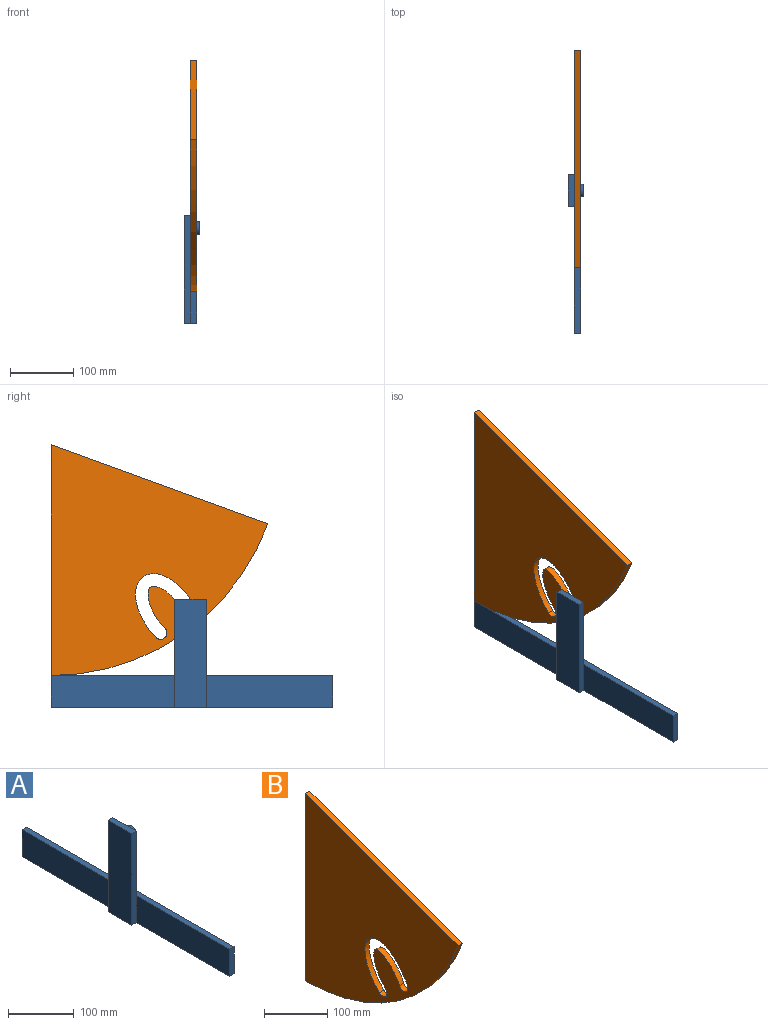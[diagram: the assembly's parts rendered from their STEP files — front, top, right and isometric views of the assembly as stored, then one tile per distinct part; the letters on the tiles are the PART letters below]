
ASSEMBLY  parts=2 mates=1
PART A: 14 faces, bbox 25x444.9x170 mm
  f0: plane 199.88x50mm, normal (-1,0,0), area 9994mm2, adj f2,f3,f4,f8
  f1: plane 50x10mm, normal (0,1,0), area 500mm2, adj f2,f4,f5,f6
  f2: plane 444.88x10mm, normal (0,0,1), area 4448.8mm2, adj f0,f1,f3,f5,f6,f11
  f3: plane 50x10mm, normal (0,-1,0), area 500mm2, adj f0,f2,f4,f6
  f4: plane 444.88x20mm, normal (0,0,-1), area 4948.8mm2, adj f0,f1,f3,f5,f6,f7,f8,f10
  f5: plane 195x50mm, normal (-1,0,0), area 9750mm2, adj f1,f2,f4,f7
  f6: plane 444.88x50mm, normal (1,0,0), area 22244mm2, adj f1,f2,f3,f4
  f7: plane 170x10mm, normal (0,1,0), area 1700mm2, adj f4,f5,f9,f10,f11
  f8: plane 170x10mm, normal (0,-1,0), area 1700mm2, adj f0,f4,f9,f10,f11
  f9: plane 50x10mm, normal (0,0,1), area 500mm2, adj f7,f8,f10,f11
  f10: plane 170x50mm, normal (-1,0,0), area 8500mm2, adj f4,f7,f8,f9
  f11: plane 120x50mm, normal (1,0,0), area 5685.8mm2, adj f2,f7,f8,f9,f12
  f12: cylinder r=10mm len=20mm, axis (-1,0,0), area 942.5mm2, adj f11,f13
  f13: plane 20x20mm, normal (1,0,0), area 314.2mm2, adj f12
PART B: 9 faces, bbox 10x342.2x364.1 mm
  f0: cylinder r=364.14mm len=342.18mm, axis (1,0,0), area 4448.8mm2, adj f1,f2,f3,f4
  f1: plane 364.14x10mm, normal (0,1,0), area 3641.4mm2, adj f0,f2,f3,f4
  f2: plane 342.18x124.54mm, normal (0,-0.34,0.94), area 3641.4mm2, adj f0,f1,f3,f4
  f3: plane 364.14x342.18mm, normal (-1,0,0), area 77018.5mm2, adj f0,f1,f2,f5,f6,f7,f8
  f4: plane 364.14x342.18mm, normal (1,0,0), area 77018.5mm2, adj f0,f1,f2,f5,f6,f7,f8
  f5: extruded ~66.65x57.63mm, area 1483.2mm2, adj f3,f4,f6,f8
  f6: cylinder r=10mm len=17.14mm, axis (1,0,0), area 314.2mm2, adj f3,f4,f5,f7
  f7: extruded ~100.92x95.82mm, area 2185.2mm2, adj f3,f4,f6,f8
  f8: cylinder r=10mm len=19.1mm, axis (1,0,0), area 314.2mm2, adj f3,f4,f5,f7
PLACE A t=(0,-386.52,262.28)mm fixed
PLACE B t=(0,-386.52,262.28)mm
MATE planar B.f4 <-> A.f6  axis (1,0,0) through (0,-515.06,442.84)mm
